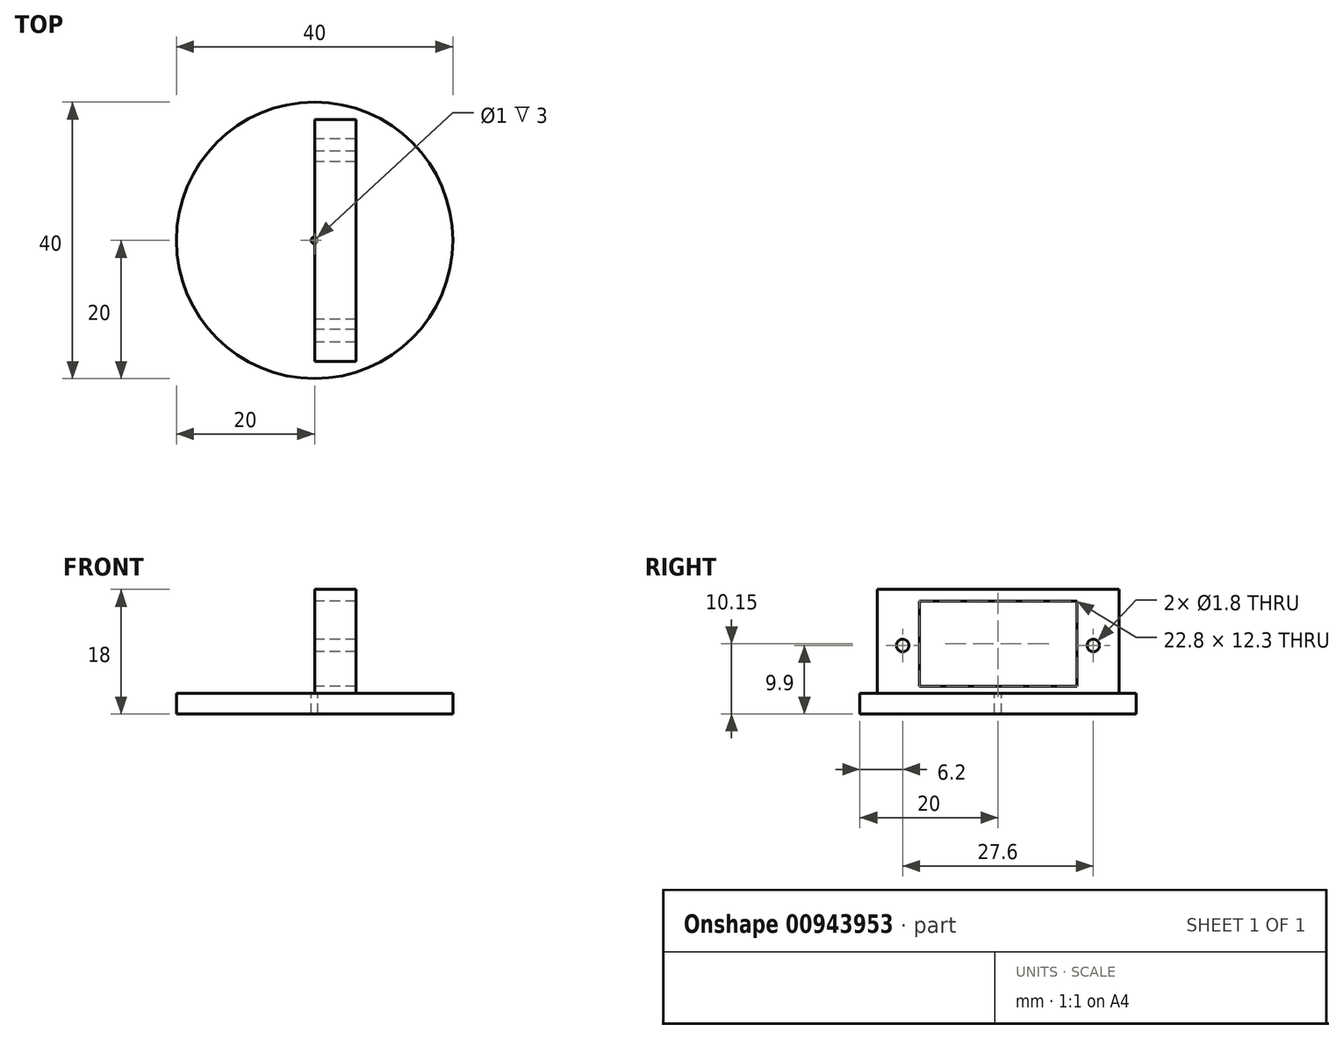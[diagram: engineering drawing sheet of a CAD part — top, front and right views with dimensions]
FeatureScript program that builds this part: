
annotation { "Feature Type Name" : "Feature", "Feature Type Description" : "" }
export const myFeature = defineFeature(function(context is Context, id is Id, definition is map)
    precondition{}
    {
        {
            var Q0;
            Q0=qCreatedBy(makeId("Right.planeOp"),FACE);
            var sketch = newSketch(context, id + "F0", { "sketchPlane" : qUnion([Q0])});
            skLineSegment(sketch, "E0.right", {"start": v(-16.1, 5.9) * mm, "end": v(-16.1, -5.9) * mm, "construction": true});
            skPoint(sketch, "E0.middle", {"position": v(0, 0) * mm});
            skLineSegment(sketch, "E1.bottom", {"start": v(-16.1, 5.9) * mm, "end": v(-11.4, 5.9) * mm, "construction": true});
            skLineSegment(sketch, "E2.right", {"start": v(11.4, 5.9) * mm, "end": v(11.4, -5.9) * mm});
            skLineSegment(sketch, "E3.right", {"start": v(3.3, 5.9) * mm, "end": v(3.3, -5.9) * mm, "construction": true});
            skCircle(sketch, "E4", {"center": v(-5.5, 0) * mm, "radius": 2.3 * mm, "construction": true});
            skLineSegment(sketch, "E5", {"start": v(-16.1, 0) * mm, "end": v(-13.8, 0) * mm, "construction": true});
            skLineSegment(sketch, "E6", {"start": v(16.1, 0) * mm, "end": v(13.8, 0) * mm, "construction": true});
            skCircle(sketch, "E7", {"center": v(13.8, 0) * mm, "radius": 0.9 * mm});
            skLineSegment(sketch, "E8", {"start": v(11.4, 5.9) * mm, "end": v(16.1, 5.9) * mm, "construction": true});
            skLineSegment(sketch, "E9.right", {"start": v(17.5, 5.6) * mm, "end": v(17.5, -6.9) * mm});
            skLineSegment(sketch, "E10", {"start": v(16.1, -5.9) * mm, "end": v(16.1, 5.9) * mm, "construction": true});
            skLineSegment(sketch, "E11", {"start": v(11.4, -5.9) * mm, "end": v(16.1, -5.9) * mm, "construction": true});
            skPoint(sketch, "E12.orphan", {"position": v(-16.1, 5.9) * mm});
            skLineSegment(sketch, "E13", {"start": v(-11.4, 5.9) * mm, "end": v(-11.4, -5.9) * mm});
            skLineSegment(sketch, "E14", {"start": v(-16.1, -5.9) * mm, "end": v(-11.4, -5.9) * mm, "construction": true});
            skLineSegment(sketch, "E15", {"start": v(-11.4, -5.9) * mm, "end": v(11.4, -5.9) * mm});
            skPoint(sketch, "E16.0.midPoint", {"position": v(-11.8, 0) * mm});
            skPoint(sketch, "E17.0.midPoint", {"position": v(15.8, 0) * mm});
            skLineSegment(sketch, "E18.bottom", {"start": v(17.5, -6.9) * mm, "end": v(-17.5, -6.9) * mm});
            skLineSegment(sketch, "E18.left", {"start": v(17.5, -6.9) * mm, "end": v(17.5, 6.9) * mm});
            skLineSegment(sketch, "E18.right", {"start": v(-17.5, -6.9) * mm, "end": v(-17.5, 6.9) * mm});
            skLineSegment(sketch, "E19.top", {"start": v(-17.5, 8.1) * mm, "end": v(17.5, 8.1) * mm});
            skLineSegment(sketch, "E19.left", {"start": v(-17.5, 6.9) * mm, "end": v(-17.5, 8.1) * mm});
            skLineSegment(sketch, "E19.right", {"start": v(17.5, 6.9) * mm, "end": v(17.5, 8.1) * mm});
            skLineSegment(sketch, "E20.bottom", {"start": v(-11.4, 5.9) * mm, "end": v(11.4, 5.9) * mm, "construction": true});
            skLineSegment(sketch, "E20.top", {"start": v(-11.4, 6.4) * mm, "end": v(11.4, 6.4) * mm});
            skLineSegment(sketch, "E20.left", {"start": v(-11.4, 5.9) * mm, "end": v(-11.4, 6.4) * mm});
            skLineSegment(sketch, "E20.right", {"start": v(11.4, 5.9) * mm, "end": v(11.4, 6.4) * mm});
            skCircle(sketch, "E21", {"center": v(-13.8, 0) * mm, "radius": 0.9 * mm});
            skSolve(sketch);
        }
        {
            var Q0;
            Q0=makeQuery(id+"F0.imprint","IMPRINT",FACE,{"disambiguationData":[TD([[makeQuery(id+"F0.imprint","IMPRINT",EDGE,{"derivedFrom":sQuery(id+"F0.wireOp",EDGE,"E2.right")}),1.0]])]});
            extrude(context, id + "F1", {"entities" : qUnion([Q0]), "depth" : 6 * mm, "offsetDistance" : 25 * mm});
        }
        {
            var Q0;
            Q0=makeQuery(id+"F1.opExtrude","SWEPT_FACE",FACE,{"disambiguationData":[OSD([sQuery(id+"F0.wireOp",EDGE,"E18.bottom")])]});
            var sketch = newSketch(context, id + "F2", { "sketchPlane" : qUnion([Q0])});
            skCircle(sketch, "E22", {"center": v(0, 0) * mm, "radius": 20 * mm});
            skCircle(sketch, "E23", {"center": v(0, 0) * mm, "radius": 0.5 * mm});
            skSolve(sketch);
        }
        {
            var Q0;
            Q0 = qSketchRegion(id + "F2", true);
            extrude(context, id + "F3", {"entities" : qUnion([Q0]), "operationType" : NewBodyOperationType.ADD, "depth" : 3 * mm, "offsetDistance" : 25 * mm});
        }
    });
